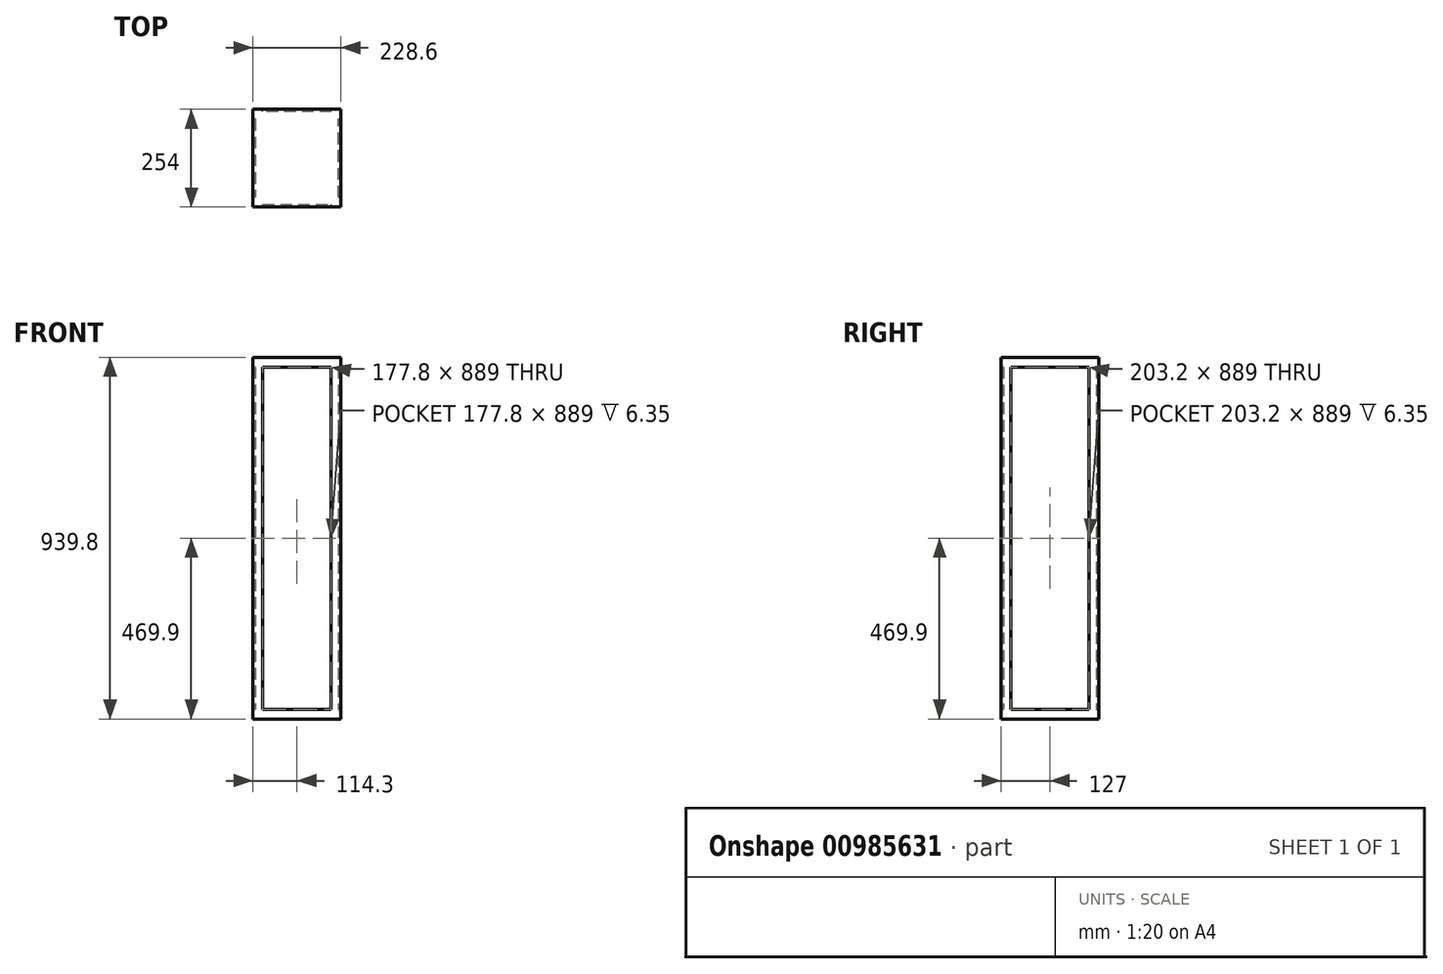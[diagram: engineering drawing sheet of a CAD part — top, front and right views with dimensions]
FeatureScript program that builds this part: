
annotation { "Feature Type Name" : "Feature", "Feature Type Description" : "" }
export const myFeature = defineFeature(function(context is Context, id is Id, definition is map)
    precondition{}
    {
        {
            var Q0;
            Q0=qCreatedBy(makeId("Top.planeOp"),FACE);
            var sketch = newSketch(context, id + "F0", { "sketchPlane" : qUnion([Q0])});
            skLineSegment(sketch, "E0.bottom", {"start": v(114.3, 127) * mm, "end": v(-114.3, 127) * mm});
            skLineSegment(sketch, "E0.top", {"start": v(114.3, -127) * mm, "end": v(-114.3, -127) * mm});
            skLineSegment(sketch, "E0.left", {"start": v(114.3, 127) * mm, "end": v(114.3, -127) * mm});
            skLineSegment(sketch, "E0.right", {"start": v(-114.3, 127) * mm, "end": v(-114.3, -127) * mm});
            skPoint(sketch, "E0.middle", {"position": v(0, 0) * mm});
            skSolve(sketch);
        }
        {
            var Q0;
            Q0=makeQuery(id+"F0.imprint","IMPRINT",FACE,{"disambiguationData":[TD([[makeQuery(id+"F0.imprint","IMPRINT",EDGE,{"derivedFrom":sQuery(id+"F0.wireOp",EDGE,"E0.bottom")}),1.0]])]});
            extrude(context, id + "F1", {"entities" : qUnion([Q0]), "depth" : 939.8 * mm, "offsetDistance" : 25.4 * mm});
        }
        {
            var Q0;
            Q0=makeQuery(id+"F1.opExtrude","SWEPT_FACE",FACE,{"disambiguationData":[OSD([sQuery(id+"F0.wireOp",EDGE,"E0.top")])]});
            var sketch = newSketch(context, id + "F2", { "sketchPlane" : qUnion([Q0])});
            skLineSegment(sketch, "E1.0", {"start": v(-88.9, 25.4) * mm, "end": v(88.9, 25.4) * mm});
            skLineSegment(sketch, "E1.1", {"start": v(-88.9, 914.4) * mm, "end": v(-88.9, 25.4) * mm});
            skLineSegment(sketch, "E1.2", {"start": v(88.9, 914.4) * mm, "end": v(-88.9, 914.4) * mm});
            skLineSegment(sketch, "E1.3", {"start": v(88.9, 25.4) * mm, "end": v(88.9, 914.4) * mm});
            skSolve(sketch);
        }
        {
            var Q0;
            Q0=makeQuery(id+"F2.imprint","IMPRINT",FACE,{"disambiguationData":[TD([[makeQuery(id+"F2.imprint","IMPRINT",EDGE,{"derivedFrom":sQuery(id+"F2.wireOp",EDGE,"E1.0")}),1.0]])]});
            extrude(context, id + "F3", {"entities" : qUnion([Q0]), "operationType" : NewBodyOperationType.REMOVE, "oppositeDirection" : true, "depth" : 6.35 * mm, "offsetDistance" : 25.4 * mm});
        }
        {
            var Q0;
            Q0=makeQuery(id+"F1.opExtrude","SWEPT_FACE",FACE,{"disambiguationData":[OSD([sQuery(id+"F0.wireOp",EDGE,"E0.left")])]});
            var sketch = newSketch(context, id + "F4", { "sketchPlane" : qUnion([Q0])});
            skLineSegment(sketch, "E2.0", {"start": v(-101.6, 25.4) * mm, "end": v(101.6, 25.4) * mm});
            skLineSegment(sketch, "E2.1", {"start": v(-101.6, 914.4) * mm, "end": v(-101.6, 25.4) * mm});
            skLineSegment(sketch, "E2.2", {"start": v(101.6, 914.4) * mm, "end": v(-101.6, 914.4) * mm});
            skLineSegment(sketch, "E2.3", {"start": v(101.6, 25.4) * mm, "end": v(101.6, 914.4) * mm});
            skSolve(sketch);
        }
        {
            var Q0;
            Q0 = qSketchRegion(id + "F4", true);
            extrude(context, id + "F5", {"entities" : qUnion([Q0]), "operationType" : NewBodyOperationType.REMOVE, "oppositeDirection" : true, "depth" : 6.35 * mm, "offsetDistance" : 25.4 * mm});
        }
        {
            var Q0;
            Q0=makeQuery(id+"F1.opExtrude","SWEPT_FACE",FACE,{"disambiguationData":[OSD([sQuery(id+"F0.wireOp",EDGE,"E0.bottom")])]});
            var sketch = newSketch(context, id + "F6", { "sketchPlane" : qUnion([Q0])});
            skLineSegment(sketch, "E3.0", {"start": v(-88.9, 25.4) * mm, "end": v(88.9, 25.4) * mm});
            skLineSegment(sketch, "E3.1", {"start": v(-88.9, 914.4) * mm, "end": v(-88.9, 25.4) * mm});
            skLineSegment(sketch, "E3.2", {"start": v(88.9, 914.4) * mm, "end": v(-88.9, 914.4) * mm});
            skLineSegment(sketch, "E3.3", {"start": v(88.9, 25.4) * mm, "end": v(88.9, 914.4) * mm});
            skSolve(sketch);
        }
        {
            var Q0;
            Q0 = qSketchRegion(id + "F6", true);
            extrude(context, id + "F7", {"entities" : qUnion([Q0]), "operationType" : NewBodyOperationType.REMOVE, "oppositeDirection" : true, "depth" : 6.35 * mm, "offsetDistance" : 25.4 * mm});
        }
        {
            var Q0;
            Q0=makeQuery(id+"F1.opExtrude","SWEPT_FACE",FACE,{"disambiguationData":[OSD([sQuery(id+"F0.wireOp",EDGE,"E0.right")])]});
            var sketch = newSketch(context, id + "F8", { "sketchPlane" : qUnion([Q0])});
            skLineSegment(sketch, "E4.0", {"start": v(-101.6, 25.4) * mm, "end": v(101.6, 25.4) * mm});
            skLineSegment(sketch, "E4.1", {"start": v(-101.6, 914.4) * mm, "end": v(-101.6, 25.4) * mm});
            skLineSegment(sketch, "E4.2", {"start": v(101.6, 914.4) * mm, "end": v(-101.6, 914.4) * mm});
            skLineSegment(sketch, "E4.3", {"start": v(101.6, 25.4) * mm, "end": v(101.6, 914.4) * mm});
            skSolve(sketch);
        }
        {
            var Q0;
            Q0 = qSketchRegion(id + "F8", true);
            extrude(context, id + "F9", {"entities" : qUnion([Q0]), "operationType" : NewBodyOperationType.REMOVE, "oppositeDirection" : true, "depth" : 6.35 * mm, "offsetDistance" : 25.4 * mm});
        }
    });
